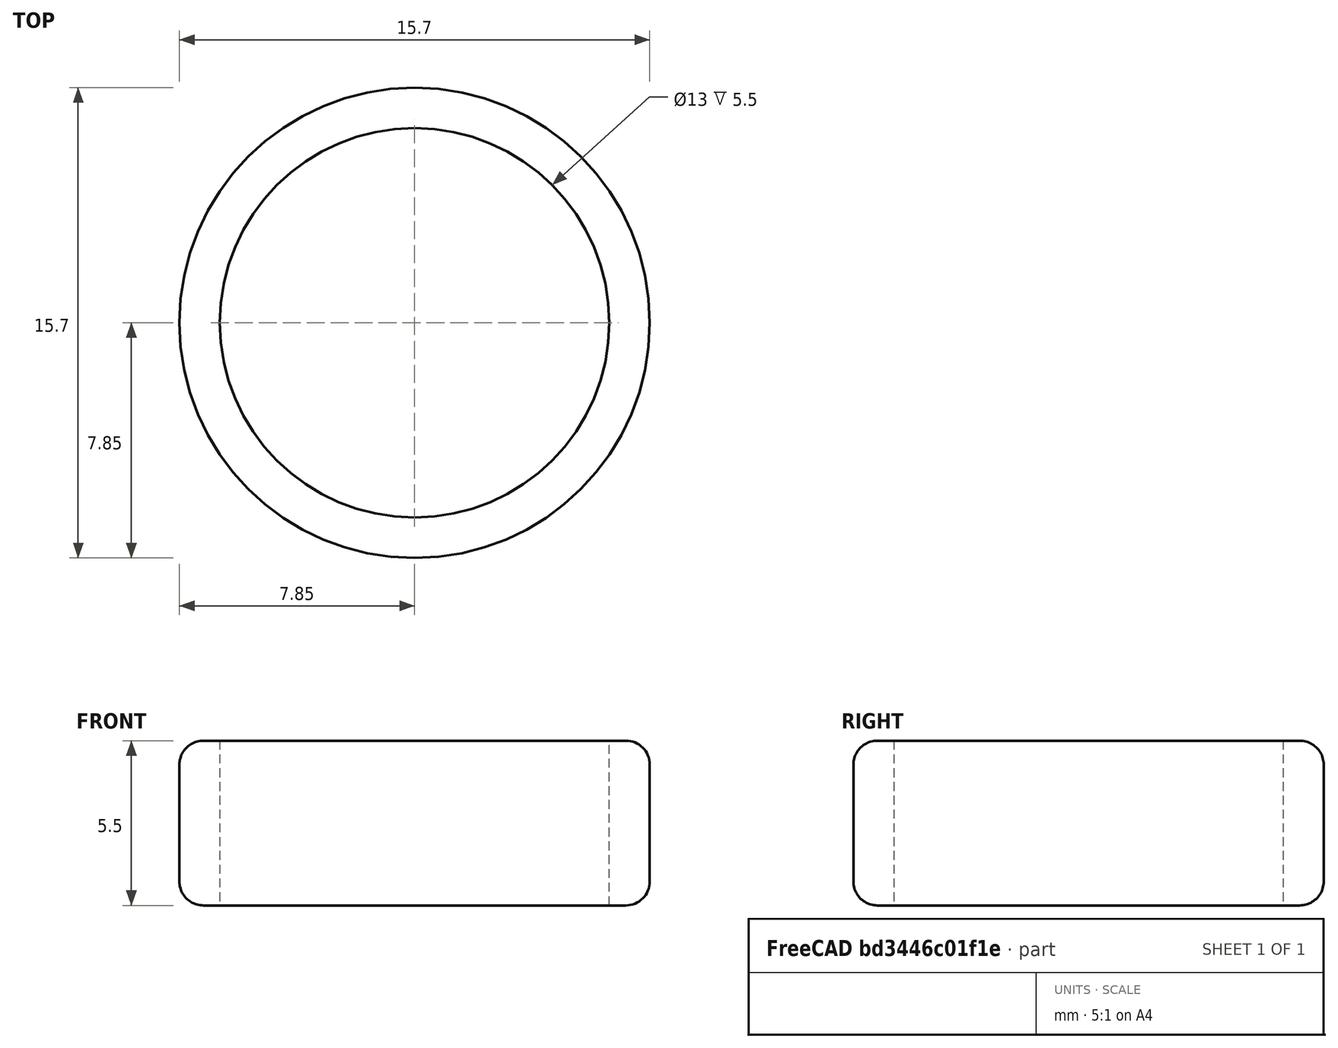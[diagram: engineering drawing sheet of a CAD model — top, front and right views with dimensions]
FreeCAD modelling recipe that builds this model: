
FCSTD DOCUMENT  (FreeCAD 0.18.1R)
Label: Pneu_J13x6
License: All rights reserved
LicenseURL: http://en.wikipedia.org/wiki/All_rights_reserved
objects: Sketcher::SketchObject×1, PartDesign::Pad×1, PartDesign::Fillet×1, PartDesign::Body×1
note: 5 computed .brp shape members not serialized (recipe doc carries the construction recipe); baked Part::Feature solids carry a one-line shape summary decoded from their .brp

FEATURE [Sketcher::SketchObject] Sketch
  MapMode = 5
  Support = -> [XY_Plane]
  sketch-geometry (2):
    g0: Circle CenterX=0 CenterY=0 CenterZ=0 NormalX=0 NormalY=0 NormalZ=1 AngleXU=0 Radius=6.5
    g1: Circle CenterX=0 CenterY=0 CenterZ=0 NormalX=0 NormalY=0 NormalZ=1 AngleXU=0 Radius=7.85
  constraints (4):
    c: Coincident(g0,g-1)
    c: Radius(g0) = 6.5
    c: Coincident(g1,g-1)
    c: Radius(g1) = 7.85
FEATURE [PartDesign::Pad] Pad
  Length = 5.5
  Length2 = 100
  Profile = -> Sketch
  Type = 0
FEATURE [PartDesign::Fillet] Fillet
  Base = -> Pad [Face1]
  BaseFeature = -> Pad
  Radius = 0.8
FEATURE [PartDesign::Body] Body
  Group = -> [Sketch,Pad,Fillet]
  Origin = -> Origin
  Tip = -> Fillet
